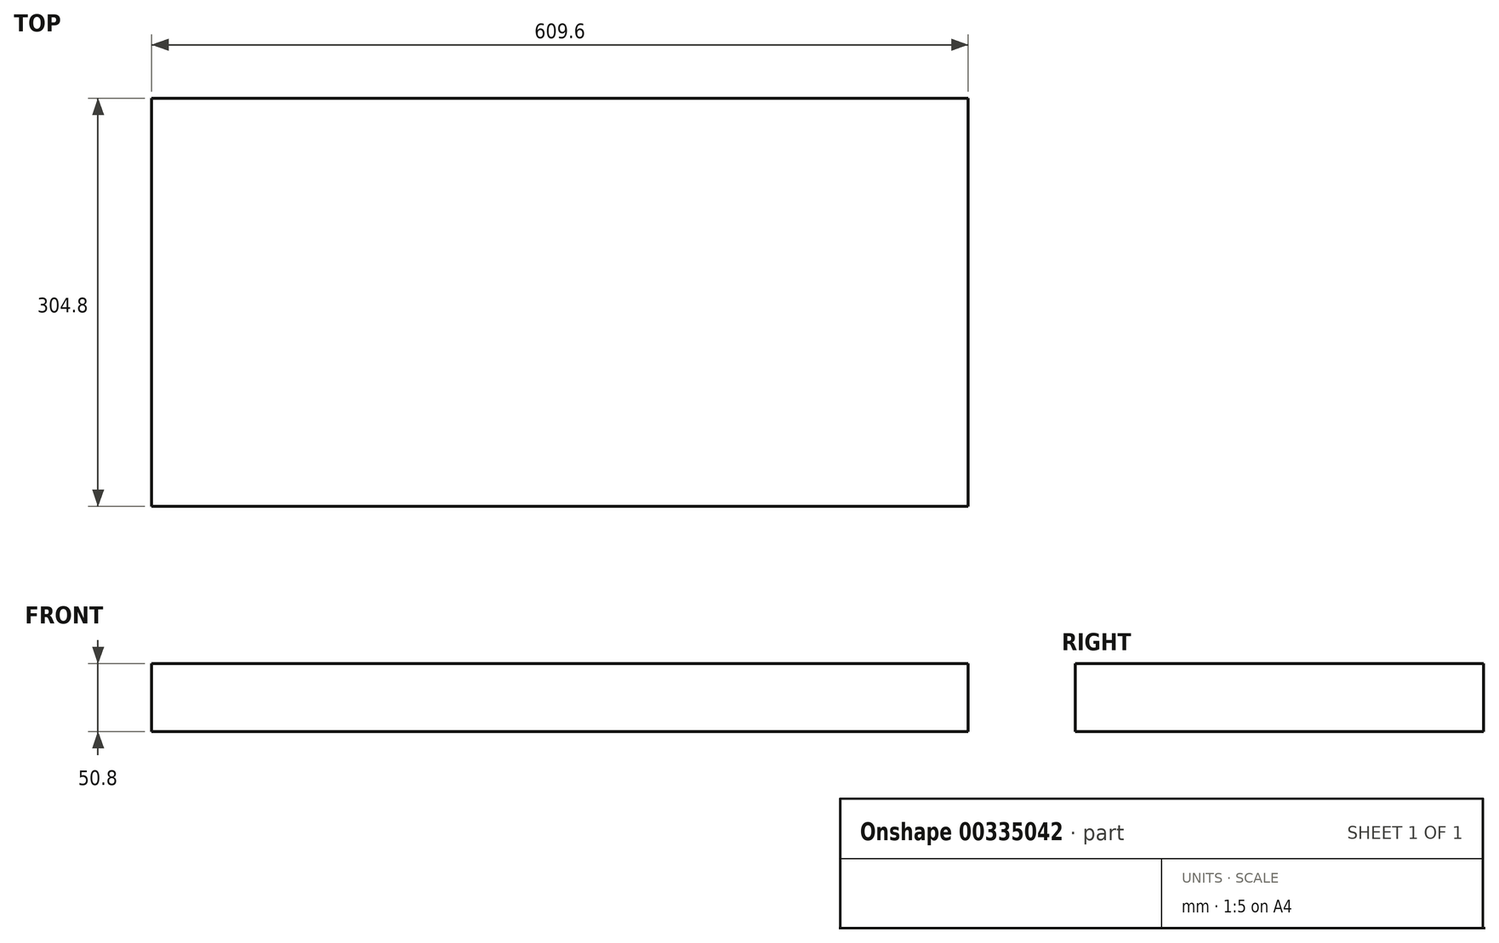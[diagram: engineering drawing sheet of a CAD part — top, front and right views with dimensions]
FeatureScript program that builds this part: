
annotation { "Feature Type Name" : "Feature", "Feature Type Description" : "" }
export const myFeature = defineFeature(function(context is Context, id is Id, definition is map)
    precondition{}
    {
        {
            var Q0;
            Q0=qCreatedBy(makeId("Top.planeOp"),FACE);
            var sketch = newSketch(context, id + "F0", { "sketchPlane" : qUnion([Q0])});
            skLineSegment(sketch, "E0.bottom", {"start": v(-162.06, 141.94) * mm, "end": v(447.54, 141.94) * mm});
            skLineSegment(sketch, "E0.top", {"start": v(-162.06, -162.86) * mm, "end": v(447.54, -162.86) * mm});
            skLineSegment(sketch, "E0.left", {"start": v(-162.06, 141.94) * mm, "end": v(-162.06, -162.86) * mm});
            skLineSegment(sketch, "E0.right", {"start": v(447.54, 141.94) * mm, "end": v(447.54, -162.86) * mm});
            skSolve(sketch);
        }
        {
            var Q0;
            Q0 = qSketchRegion(id + "F0", true);
            extrude(context, id + "F1", {"entities" : qUnion([Q0]), "depth" : 50.8 * mm});
        }
    });
